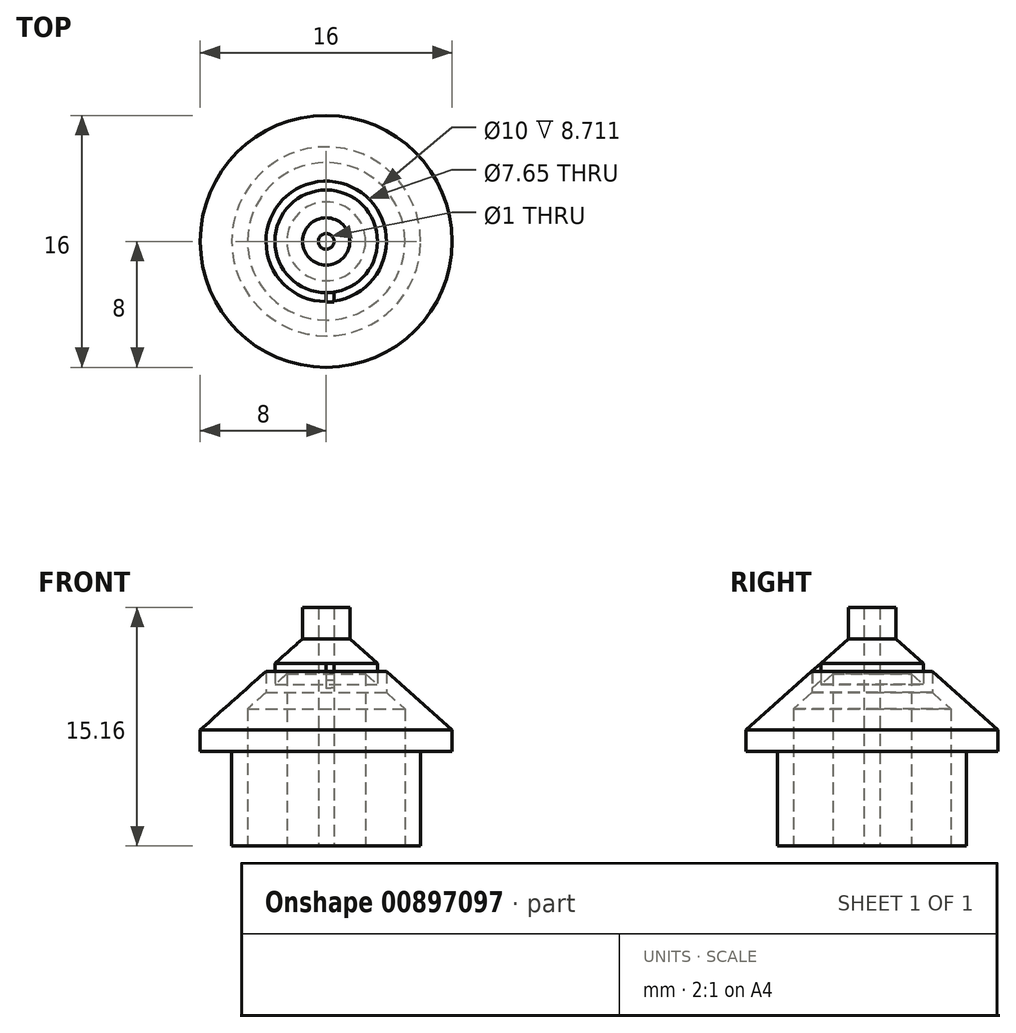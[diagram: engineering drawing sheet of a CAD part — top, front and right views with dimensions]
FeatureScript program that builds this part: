
annotation { "Feature Type Name" : "Feature", "Feature Type Description" : "" }
export const myFeature = defineFeature(function(context is Context, id is Id, definition is map)
    precondition{}
    {
        {
            var Q0;
            Q0=qCreatedBy(makeId("Front.planeOp"),FACE);
            var sketch = newSketch(context, id + "F0", { "sketchPlane" : qUnion([Q0])});
            skLineSegment(sketch, "E0", {"start": v(0, -7.66) * mm, "end": v(0, 10.41) * mm, "construction": true});
            skLineSegment(sketch, "E1", {"start": v(-6, 0) * mm, "end": v(-6, 6) * mm});
            skLineSegment(sketch, "E2", {"start": v(-6, 6) * mm, "end": v(-8, 6) * mm});
            skLineSegment(sketch, "E3", {"start": v(-8, 6) * mm, "end": v(-8, 7.38) * mm});
            skLineSegment(sketch, "E4", {"start": v(-8, 7.38) * mm, "end": v(-3.82, 11.1) * mm});
            skLineSegment(sketch, "E5", {"start": v(-1.5, 13.16) * mm, "end": v(-1.5, 15.16) * mm});
            skLineSegment(sketch, "E6", {"start": v(-1.5, 15.16) * mm, "end": v(-0.5, 15.16) * mm});
            skLineSegment(sketch, "E7", {"start": v(-0.5, 15.16) * mm, "end": v(-0.5, 12.71) * mm});
            skLineSegment(sketch, "E8", {"start": v(-2.5, 10.93) * mm, "end": v(-3.26, 10.26) * mm});
            skLineSegment(sketch, "E9", {"start": v(-5, 8.71) * mm, "end": v(-5, 0) * mm});
            skLineSegment(sketch, "E10", {"start": v(-5, 0) * mm, "end": v(-6, 0) * mm});
            skLineSegment(sketch, "E11", {"start": v(-0.5, 12.71) * mm, "end": v(-0.5, 0) * mm});
            skLineSegment(sketch, "E12", {"start": v(-0.5, 0) * mm, "end": v(-2.5, 0) * mm});
            skLineSegment(sketch, "E13", {"start": v(-2.5, 0) * mm, "end": v(-2.5, 10.93) * mm});
            skLineSegment(sketch, "E14", {"start": v(-3.82, 9.76) * mm, "end": v(-3.82, 11.1) * mm});
            skLineSegment(sketch, "E15", {"start": v(-3.26, 10.26) * mm, "end": v(-3.26, 11.6) * mm});
            skLineSegment(sketch, "E16.trimOffspring", {"start": v(-3.26, 11.6) * mm, "end": v(-1.5, 13.16) * mm});
            skLineSegment(sketch, "E17.trimOffspring", {"start": v(-3.82, 9.76) * mm, "end": v(-5, 8.71) * mm});
            skSolve(sketch);
        }
        {
            var Q0;
            Q0 = qSketchRegion(id + "F0", true);
            var Q1;
            Q1=sQuery(id+"F0.wireOp",EDGE,"E0");
            revolve(context, id + "F1", {"surfaceOperationType" : NewSurfaceOperationType.NEW, "entities" : qUnion([Q0]), "axis" : qUnion([Q1]), "revolveType" : RevolveType.FULL});
        }
        {
            var Q0;
            Q0=qCreatedBy(makeId("Right.planeOp"),FACE);
            var sketch = newSketch(context, id + "F2", { "sketchPlane" : qUnion([Q0])});
            skLineSegment(sketch, "E18.0", {"start": v(3.26, 11.6) * mm, "end": v(-3.26, 11.6) * mm});
            skLineSegment(sketch, "E19", {"start": v(-8, 7.38) * mm, "end": v(-3.84, 11.08) * mm});
            skLineSegment(sketch, "E20", {"start": v(3.82, 11.1) * mm, "end": v(8, 7.38) * mm});
            skLineSegment(sketch, "E21", {"start": v(-3.26, 11.6) * mm, "end": v(-3.84, 11.08) * mm});
            skLineSegment(sketch, "E22", {"start": v(-3.26, 10.52) * mm, "end": v(-3.84, 10) * mm});
            skLineSegment(sketch, "E23", {"start": v(-3.84, 10) * mm, "end": v(-3.84, 11.08) * mm});
            skLineSegment(sketch, "E24", {"start": v(-3.26, 11.6) * mm, "end": v(-3.26, 10.52) * mm});
            skSolve(sketch);
        }
        {
            var Q0;
            Q0=makeQuery(id+"F2.imprint","IMPRINT",FACE,{"disambiguationData":[TD([[makeQuery(id+"F2.imprint","IMPRINT",EDGE,{"derivedFrom":sQuery(id+"F2.wireOp",EDGE,"E21")}),1.0]])]});
            extrude(context, id + "F3", {"entities" : qUnion([Q0]), "operationType" : NewBodyOperationType.ADD, "depth" : 0.5 * mm, "offsetDistance" : 25.4 * mm});
        }
    });
